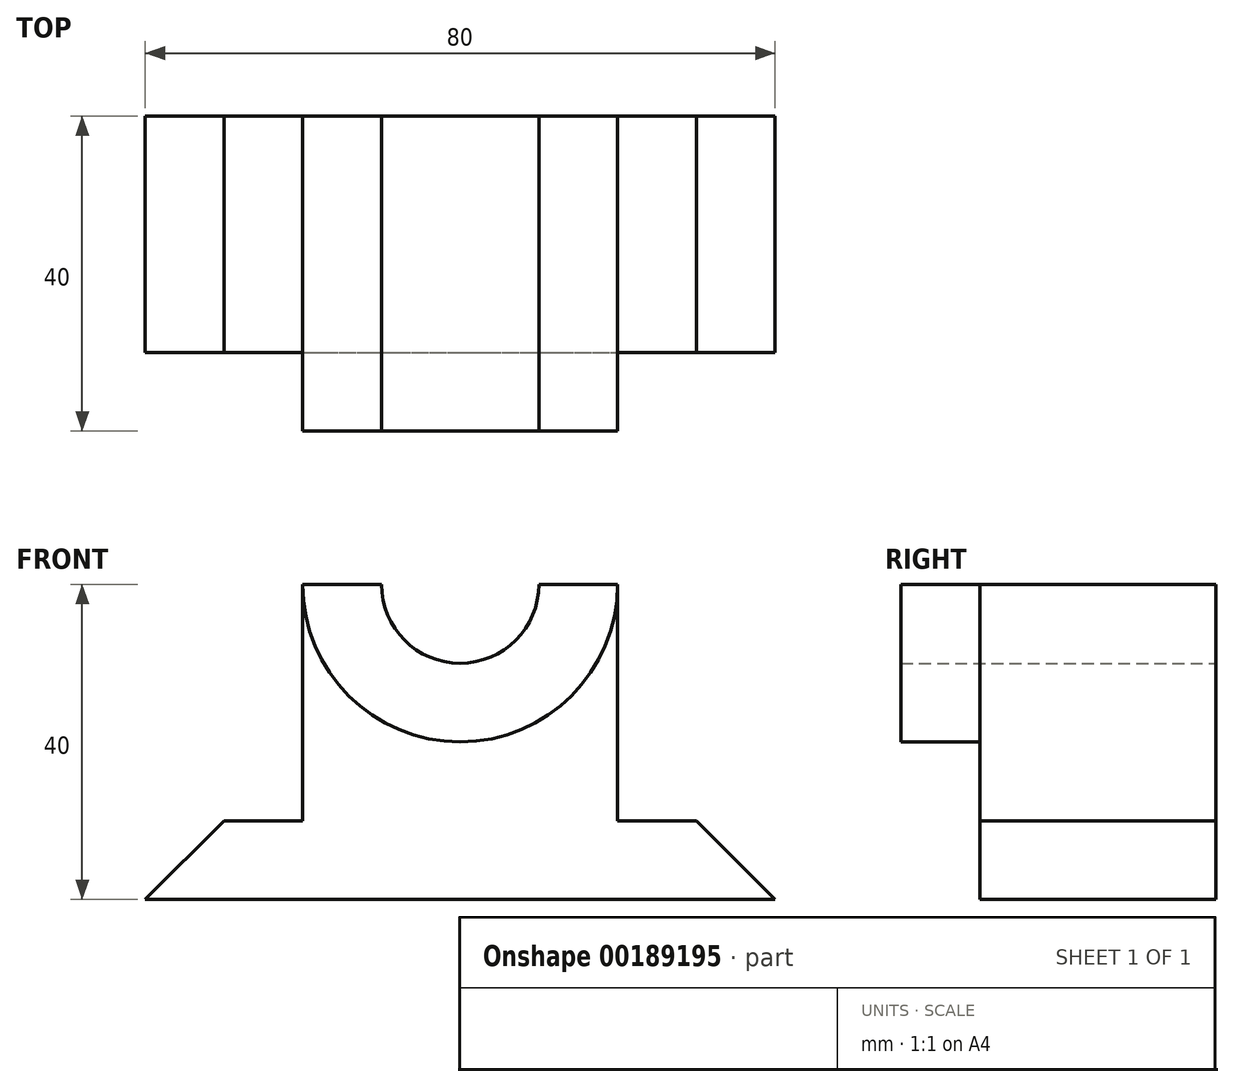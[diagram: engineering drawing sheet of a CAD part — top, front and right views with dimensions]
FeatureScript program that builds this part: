
annotation { "Feature Type Name" : "Feature", "Feature Type Description" : "" }
export const myFeature = defineFeature(function(context is Context, id is Id, definition is map)
    precondition{}
    {
        {
            var Q0;
            Q0=qCreatedBy(makeId("Front.planeOp"),FACE);
            var sketch = newSketch(context, id + "F0", { "sketchPlane" : qUnion([Q0])});
            skLineSegment(sketch, "E0", {"start": v(-40, 0) * mm, "end": v(40, 0) * mm});
            skLineSegment(sketch, "E1", {"start": v(40, 0) * mm, "end": v(30, 10) * mm});
            skLineSegment(sketch, "E2", {"start": v(30, 10) * mm, "end": v(20, 10) * mm});
            skLineSegment(sketch, "E3", {"start": v(20, 10) * mm, "end": v(20, 40) * mm});
            skLineSegment(sketch, "E4", {"start": v(20, 40) * mm, "end": v(-20, 40) * mm});
            skLineSegment(sketch, "E5", {"start": v(-20, 40) * mm, "end": v(-20, 10) * mm});
            skLineSegment(sketch, "E6", {"start": v(-20, 10) * mm, "end": v(-30, 10) * mm});
            skLineSegment(sketch, "E7", {"start": v(-30, 10) * mm, "end": v(-40, 0) * mm});
            skSolve(sketch);
        }
        {
            var Q0;
            Q0=makeQuery(id+"F0.imprint","IMPRINT",FACE,{"disambiguationData":[TD([[makeQuery(id+"F0.imprint","IMPRINT",EDGE,{"derivedFrom":sQuery(id+"F0.wireOp",EDGE,"E0")}),1.0]])]});
            extrude(context, id + "F1", {"entities" : qUnion([Q0]), "depth" : 30 * mm});
        }
        {
            var Q0;
            Q0=makeQuery(id+"F1.opExtrude","CAP_FACE",FACE,{"disambiguationData":[OSD([sQuery(id+"F0.wireOp",EDGE,"E0"),sQuery(id+"F0.wireOp",EDGE,"E1"),sQuery(id+"F0.wireOp",EDGE,"E2"),sQuery(id+"F0.wireOp",EDGE,"E3"),sQuery(id+"F0.wireOp",EDGE,"E4"),sQuery(id+"F0.wireOp",EDGE,"E5"),sQuery(id+"F0.wireOp",EDGE,"E6"),sQuery(id+"F0.wireOp",EDGE,"E7")])],"isStart":false});
            var sketch = newSketch(context, id + "F2", { "sketchPlane" : qUnion([Q0])});
            skArc(sketch, "E8", {"start": v(-20, 40) * mm, "mid": v(0, 20) * mm, "end": v(20, 40) * mm});
            skArc(sketch, "E9.0", {"start": v(-10, 40) * mm, "mid": v(0, 30) * mm, "end": v(10, 40) * mm});
            skLineSegment(sketch, "E10", {"start": v(-20, 40) * mm, "end": v(20, 40) * mm});
            skSolve(sketch);
        }
        {
            var Q0;
            {var subQ0=sQuery(id+"F2.wireOp",EDGE,"E8");Q0=makeQuery(id+"F2.imprint","IMPRINT",FACE,{"disambiguationData":[TD([[makeQuery(id+"F2.imprint","IMPRINT",EDGE,{"derivedFrom":subQ0}),1.0]])]});}
            extrude(context, id + "F3", {"entities" : qUnion([Q0]), "operationType" : NewBodyOperationType.ADD, "depth" : 10 * mm});
        }
        {
            var Q0;
            {var subQ0=sQuery(id+"F0.wireOp",EDGE,"E4");var subQ1=sQuery(id+"F2.wireOp",EDGE,"E9.0");var subQ4=sQuery(id+"F0.wireOp",EDGE,"E3");var subQ5=sQuery(id+"F0.wireOp",EDGE,"E5");Q0=makeQuery(id+"F3.boolean.opBoolean","SPLIT",FACE,{"disambiguationData":[TD([makeQuery(id+"F3.opExtrude","SWEPT_FACE",FACE,{"disambiguationData":[OSD([subQ1])]})])],"derivedFrom":makeQuery(id+"F1.opExtrude","CAP_FACE",FACE,{"disambiguationData":[OSD([sQuery(id+"F0.wireOp",EDGE,"E0"),sQuery(id+"F0.wireOp",EDGE,"E1"),sQuery(id+"F0.wireOp",EDGE,"E2"),subQ4,subQ0,subQ5,sQuery(id+"F0.wireOp",EDGE,"E6"),sQuery(id+"F0.wireOp",EDGE,"E7")])],"isStart":false})});}
            extrude(context, id + "F4", {"entities" : qUnion([Q0]), "operationType" : NewBodyOperationType.REMOVE, "endBound" : BoundingType.UP_TO_NEXT, "oppositeDirection" : true, "depth" : 25 * mm});
        }
    });
